# Revit family: PRD_FrankeWS_PllrTps_Socket_ACSX1001
name_source: partatom
category: Specialty Equipment
revit_build: Autodesk Revit 2018 (Build: 20190510_1515(x64)
units: mm (PartAtom-declared; Revit-internal decimal feet)

## family parameters
Always vertical = Yes
Cut with Voids When Loaded = No
OmniClass Number = 23.45.05.14.99
OmniClass Title = Other Sanitary Washing Plumbing Fixtures
Part Type = Normal
Room Calculation Point = No
Round Connector Dimension = Use Diameter
Shared = No
Work Plane-Based = Yes

## types (1)
- ACSX1001
    AssetType = Fixed
    BIMObjectName = PRD_AR_PillarTaps_Socket_ACSX1001
    BodyMaterial = PRD_AR_ChromatedBrass_HighPolished
    Category = Pr_40_20_87_60, Pillar taps
    Default Elevation = 1219 mm
    Description = Socket for heightening of fitting housing at 140 mm, for F5S self-closing pillar taps and pillar mixer. Polished chromium-plated brass.
    DurationUnit = year
    Features = 140 mm, polished chromium-plated brass
    Finish = polished chrome
    GrossWeight = 1.03 kg
    IfcExportAs = IfcSanitaryTerminalType
    IfcExportType = USERDEFINED
    Manufacturer = KWC Group AG
    ManufacturerName = KWC Group AG
    ManufacturerURL = www.kwc.com
    Material = brass
    Model = ACSX1001
    ModelNumber = 2030041519
    ModelReference = ACSX1001
    Name = Socket ACSX1001
    NetWeight = 0.98 kg
    NominalDepth = 55 mm  [stored 0.180446 ft]
    NominalHeight = 140 mm  [stored 0.459318 ft]
    NominalLength = 0 mm  [stored 0 ft]
    NominalWidth = 50 mm  [stored 0.164042 ft]
    ProductCode = 208.0599.910
    ProductInformation = https://pim.kwc.com
    Quantity = 1
    QuantityUom = Piece
    Shape = cylinder
    Status = New
    URL = www.kwc.com
    Uniclass2015Code = Pr_40_20_87_60
    Uniclass2015Title = Pillar taps
    Uniclass2015Version = Products v1.17
    Version = 1
    WarrantyDurationUnit = year

note: [stored X ft] marks values corroborated as IEEE doubles in the binary element streams (Revit-internal decimal feet)

## geometry (parser evidence)
native form markers: Sweep x3
no freeform markers — native parametric forms only
